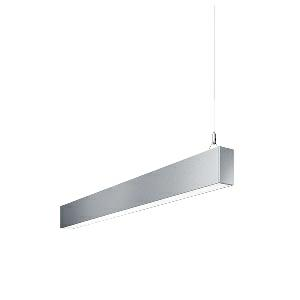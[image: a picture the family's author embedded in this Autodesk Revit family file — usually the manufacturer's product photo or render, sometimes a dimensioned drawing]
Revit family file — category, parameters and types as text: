
# Revit family: idoo_line_-_ilp_3000_830_d_end_00805728_2c00
name_source: partatom
category: Lighting Fixtures
units: mm (PartAtom-declared; Revit-internal decimal feet)

## family parameters
Cut with Voids When Loaded = No
Host = Face
Light Source = No
Part Type = Normal
Room Calculation Point = No
Round Connector Dimension = Use Diameter
Shared = No

## types (1)
- IDOO.line - ILP 3000/830/D END (1 x LED, 3000 lm, 3000K)
    Apparent Load = 23 VA
    Approval mark = CE
    CIE Flux Codes = 66 91 98 40 100
    Color Rendering = 80-89
    Color Temperature = 3000K
    Control Gear = Electronic ballast
    Default Elevation = 1800 mm
    Description = ILP 3000/830/D|Suspended luminaire|light source: LED|connected load: 220-240 V, 50/60 Hz|Power consumption: approx. 23 W|standby: approx. 0,20|luminous flux: 3000 lm|luminous efficacy: 130 lm/W|light distribution: Direct/indirect|direct ratio: approx. 40 %|colour temperature: Warm white, ca. 3000 K|color rendering index (CRI): >= 80|chromaticity tolerance:  3 SDCM|System of protection: IP 40|technology: Continuously dimmable|luminaire body|material: Sectional aluminium|colour: Silver|lamp cover: Acrylic (PMMA), Clear|mains lead: 1,0 m With free stranded wires|Fastening: Steel cable 0.3 - 0.7 m|glare control: Prism aperture|luminance(L65): <= 2700 cd/m|unified glare rating(4H 8H): <=  16|special features: DALI Load 1x, TouchDIM - dimming via standard switch, Through-wired, up to 18 m on one mains connection, Flicker-free, Suitable as emergency lighting, Mechanical and electrical connection of the individual modules without tools|
    Frequency = 50 Hz
    Height = 110 mm
    Lamp = 1 x LED
    Lamp Light Flux = 3000 lm
    Lamp count = 1
    Length = 1128 mm
    Luminous efficacy = 130 lm/W
    Manufacturer = Waldmann
    ModVariant = No
    Model = 00805728
    Mounting Place = Ceiling
    Mounting Type = Pendant
    Number of Poles = 1
    OnlyDefault = Yes
    Power Factor = 1
    Product Name = IDOO.line - ILP 3000/830/D END
    Product group = Suspended luminaire
    ProductGroupID = 9
    Protection Class = Protection class I
    Protection Degree = IP 40
    RLX_Detail_Level = 1
    RLX_Emergency_Light_Flux = 0 lm
    RLX_Emergency_Type = 0
    RLX_Emergency_Type_DB = No
    RlxData = <blob elided: 19813 chars, md5=77871738>
    Socket = socket
    Standby Power = 0 W
    System Light Flux = 3000 lm
    System Power = 23 W
    Type Comments = Product without accessories
    Type Image = 113306000-00692582.jpg
    URL = http://relux.com
    VarID = ---
    Voltage = 230 V
    Voltage Range = 220-240 V
    Weight = 0.00 kg
    Width = 60 mm  [stored 0.19685 ft]

note: [stored X ft] marks values corroborated as IEEE doubles in the binary element streams (Revit-internal decimal feet)

## geometry (parser evidence)
native form markers: Blend x4, Sweep x14
no freeform markers — native parametric forms only
